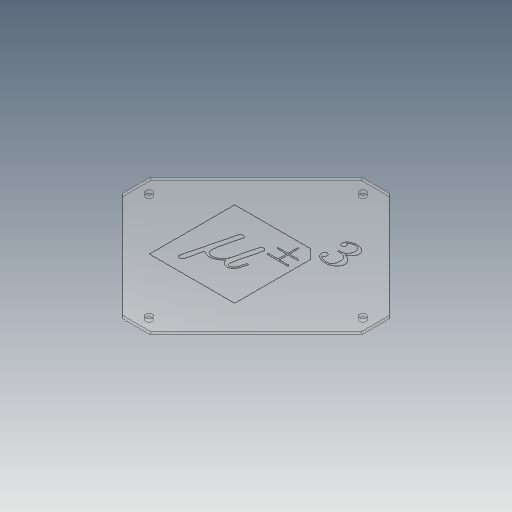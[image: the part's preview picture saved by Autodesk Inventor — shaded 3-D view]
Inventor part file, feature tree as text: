
AUTODESK INVENTOR PART (.ipt)
format: ipt  version: 2017 (Build 210142000, 142)  size: 392,192 bytes
history: native  units: mm
features: sketch x4, extrude x3, other x2, hole x1, pattern_circular x1, projected_geometry x1
ambient origin geometry x8: Origin, YZ Plane, XZ Plane, XY Plane, X Axis, Y Axis, Z Axis, Center Point
bodies: Solid1 (feature_tree)
feature tree (12):
  other  "Blocks"
  extrude  "Extrusion1"  Depth=40.0mm TaperAngle=360.0deg
  hole  "Hole1"  [1 undecoded]
  pattern_circular  "Circular Pattern1"  Count=15  [1 undecoded]
  extrude  "Extrusion2"  Depth=10.0mm TaperAngle=0.0deg
  extrude  "Extrusion3"  Depth=0.25mm TaperAngle=0.0deg
  sketch  "Sketch1"  dims[d7=2.38125mm d8=0.0mm]
  sketch  "Sketch2"  dims[d11=5.5mm d12=6.0mm d13=5.715mm d14=2.0mm d15=14.3117mm d16=8.0mm d17=20.594885mm d18=40.0mm d19=360.0deg]
  sketch  "Sketch3"  dims[d25=190.0mm d26=10.0mm d27=150.0mm]
  projected_geometry  "Projected Loop1"
  sketch  "Sketch4"  dims[d28=150.0mm d29=10.0mm d30=0.0mm d31=0.25mm d32=0.0mm]
  other  "logo"
note: 2 required parameter values undecoded (feature->parameter linkage not recoverable at this tier; creation-order binding heuristic only, values carry confidence <= 0.55)
